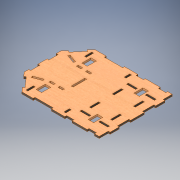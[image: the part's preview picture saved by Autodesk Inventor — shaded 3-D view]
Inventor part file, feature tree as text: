
AUTODESK INVENTOR PART (.ipt)
format: ipt  version: 2019 (Build 230136000, 136)  size: 345,088 bytes
history: native  units: mm
features: extrude x2, sketch x2, other x1
ambient origin geometry x8: Origin, YZ Plane, XZ Plane, XY Plane, X Axis, Y Axis, Z Axis, Center Point
bodies: Body1 (feature_tree)
feature tree (5):
  other  "Твердое тело1"
  extrude  "Выдавливание1"  Depth=25.0mm
  extrude  "Выдавливание2"  Depth=20.0mm
  sketch  "Эскиз1"
  sketch  "Эскиз2"
